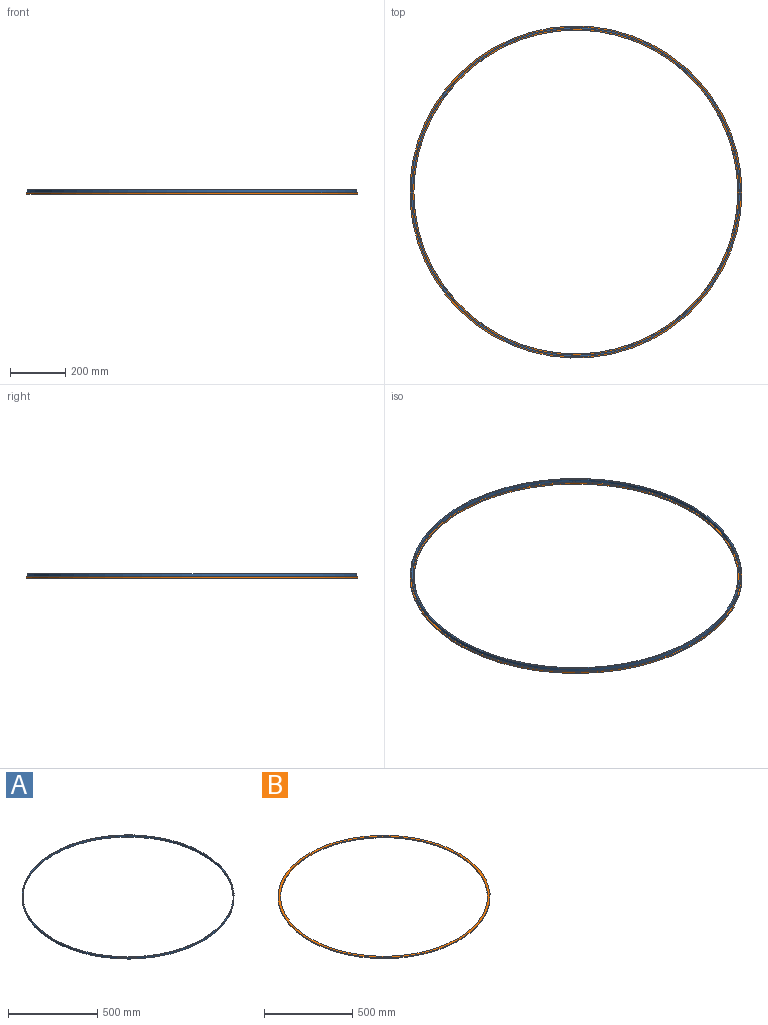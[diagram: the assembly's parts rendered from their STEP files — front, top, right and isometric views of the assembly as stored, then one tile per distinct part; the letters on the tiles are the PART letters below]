
ASSEMBLY  parts=2 mates=1
PART A: 4 faces, bbox 1190x1190x12 mm
  f0: cylinder r=595mm len=1190mm, axis (0,0,-1), area 44861.9mm2, adj f1,f2
  f1: plane 1190x1190mm, normal (0,0,1), area 18613.9mm2, adj f0,f3
  f2: plane 1190x1190mm, normal (0,0,-1), area 18613.9mm2, adj f0,f3
  f3: cylinder r=590mm len=1180mm, axis (0,0,-1), area 44485mm2, adj f1,f2
PART B: 4 faces, bbox 1200x1200x6 mm
  f0: cylinder r=600mm len=1200mm, axis (0,0,-1), area 22619.5mm2, adj f1,f2
  f1: plane 1200x1200mm, normal (0,0,1), area 55841.8mm2, adj f0,f3
  f2: plane 1200x1200mm, normal (0,0,-1), area 55841.8mm2, adj f0,f3
  f3: cylinder r=585mm len=1170mm, axis (0,0,-1), area 22054mm2, adj f1,f2
PLACE A t=(2910.47,-485.98,6)mm
PLACE B at identity
MATE fastened A.f0 <-> B.f0  axis (0,0,-1) through (-68.18,39.34,6)mm
